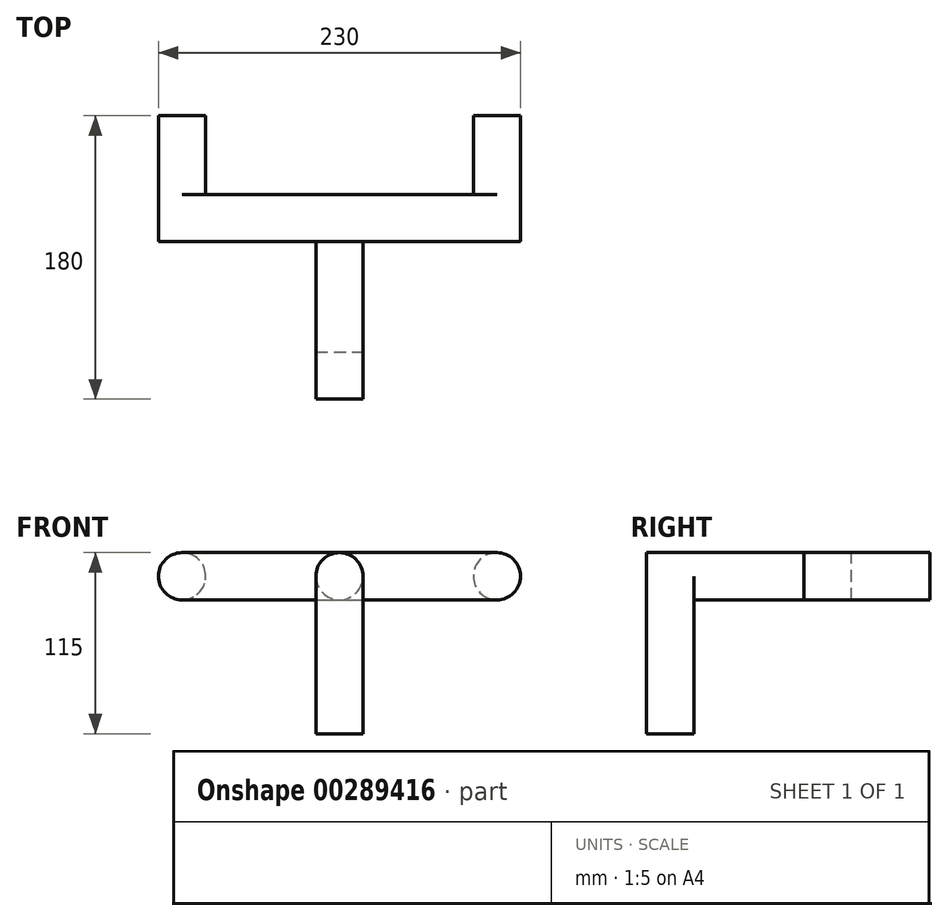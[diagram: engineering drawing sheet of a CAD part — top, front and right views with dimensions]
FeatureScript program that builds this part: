
annotation { "Feature Type Name" : "Feature", "Feature Type Description" : "" }
export const myFeature = defineFeature(function(context is Context, id is Id, definition is map)
    precondition{}
    {
        {
            var Q0;
            Q0=qCreatedBy(makeId("Front.planeOp"),FACE);
            cPlane(context, id + "F0", {"entities" : qUnion([Q0]), "cplaneType" : CPlaneType.OFFSET, "offset" : 50 * mm, "width" : 150 * mm, "height" : 150 * mm});
        }
        {
            var Q0;
            Q0=qCreatedBy(id+"F0.planeOp",FACE);
            var sketch = newSketch(context, id + "F1", { "sketchPlane" : qUnion([Q0])});
            skArc(sketch, "E0", {"start": v(-100, 15) * mm, "mid": v(-115, 0) * mm, "end": v(-100, -15) * mm});
            skArc(sketch, "E1", {"start": v(100, -15) * mm, "mid": v(115, 0) * mm, "end": v(100, 15) * mm});
            skLineSegment(sketch, "E2.bottom", {"start": v(-100, -15) * mm, "end": v(100, -15) * mm});
            skLineSegment(sketch, "E2.top", {"start": v(-100, 15) * mm, "end": v(100, 15) * mm});
            skPoint(sketch, "E2.middle", {"position": v(0, 0) * mm});
            skSolve(sketch);
        }
        {
            var Q0;
            Q0=makeQuery(id+"F1.imprint","IMPRINT",FACE,{"disambiguationData":[TD([[makeQuery(id+"F1.imprint","IMPRINT",EDGE,{"derivedFrom":sQuery(id+"F1.wireOp",EDGE,"E0")}),1.0]])]});
            extrude(context, id + "F2", {"entities" : qUnion([Q0]), "depth" : 30 * mm});
        }
        {
            var Q0;
            Q0=makeQuery(id+"F2.opExtrude","CAP_FACE",FACE,{"disambiguationData":[OSD([sQuery(id+"F1.wireOp",EDGE,"E0"),sQuery(id+"F1.wireOp",EDGE,"E1"),sQuery(id+"F1.wireOp",EDGE,"E2.bottom"),sQuery(id+"F1.wireOp",EDGE,"E2.top")])],"isStart":false});
            var sketch = newSketch(context, id + "F3", { "sketchPlane" : qUnion([Q0])});
            skCircle(sketch, "E3", {"center": v(0, 0) * mm, "radius": 15 * mm});
            skSolve(sketch);
        }
        {
            var Q0;
            {var subQ0=sQuery(id+"F3.wireOp",EDGE,"E3");var subQ1=makeQuery(id+"F3.imprint","INTERSECT",VERTEX,{"derivedFrom":[makeQuery(id+"F2.opExtrude","CAP_EDGE",EDGE,{"disambiguationData":[OSD([sQuery(id+"F1.wireOp",EDGE,"E2.bottom")])],"isStart":false}),subQ0]});Q0=makeQuery(id+"F3.imprint","IMPRINT",FACE,{"disambiguationData":[TD([[makeQuery(id+"F3.imprint","IMPRINT",EDGE,{"disambiguationData":[TD([[subQ1,1.0]])],"derivedFrom":subQ0}),1.0]])]});}
            extrude(context, id + "F4", {"entities" : qUnion([Q0]), "operationType" : NewBodyOperationType.ADD, "depth" : 100 * mm});
        }
        {
            var Q0;
            Q0=makeQuery(id+"F2.opExtrude","CAP_FACE",FACE,{"disambiguationData":[OSD([sQuery(id+"F1.wireOp",EDGE,"E0"),sQuery(id+"F1.wireOp",EDGE,"E1"),sQuery(id+"F1.wireOp",EDGE,"E2.bottom"),sQuery(id+"F1.wireOp",EDGE,"E2.top")])],"isStart":true});
            var sketch = newSketch(context, id + "F5", { "sketchPlane" : qUnion([Q0])});
            skSolve(sketch);
        }
        {
            var Q0;
            Q0=makeQuery(id+"F5.imprint","IMPRINT",FACE,{"disambiguationData":[TD([[makeQuery(id+"F5.imprint","IMPRINT",EDGE,{"derivedFrom":makeQuery(id+"F2.opExtrude","CAP_EDGE",EDGE,{"disambiguationData":[OSD([sQuery(id+"F1.wireOp",EDGE,"E0")])],"isStart":true})}),-1.0]])]});
            var sketch = newSketch(context, id + "F6", { "sketchPlane" : qUnion([Q0])});
            skCircle(sketch, "E4", {"center": v(-100, 0) * mm, "radius": 15 * mm});
            skCircle(sketch, "E5", {"center": v(100, 0) * mm, "radius": 15 * mm});
            skSolve(sketch);
        }
        {
            var Q0;
            Q0 = qSketchRegion(id + "F6", true);
            extrude(context, id + "F7", {"entities" : qUnion([Q0]), "operationType" : NewBodyOperationType.ADD, "depth" : 50 * mm});
        }
        {
            var Q0;
            Q0=qCreatedBy(makeId("Top.planeOp"),FACE);
            var sketch = newSketch(context, id + "F8", { "sketchPlane" : qUnion([Q0])});
            skLineSegment(sketch, "E6", {"start": v(0, -180) * mm, "end": v(-15, -180) * mm});
            skLineSegment(sketch, "E7", {"start": v(0, -180) * mm, "end": v(15, -180) * mm});
            skLineSegment(sketch, "E8.bottom", {"start": v(-15, -150) * mm, "end": v(15, -150) * mm});
            skLineSegment(sketch, "E8.left", {"start": v(-15, -150) * mm, "end": v(-15, -180) * mm});
            skLineSegment(sketch, "E8.right", {"start": v(15, -150) * mm, "end": v(15, -180) * mm});
            skSolve(sketch);
        }
        {
            var Q0;
            Q0 = qSketchRegion(id + "F8", true);
            extrude(context, id + "F9", {"entities" : qUnion([Q0]), "operationType" : NewBodyOperationType.ADD, "oppositeDirection" : true, "depth" : 100 * mm});
        }
    });
